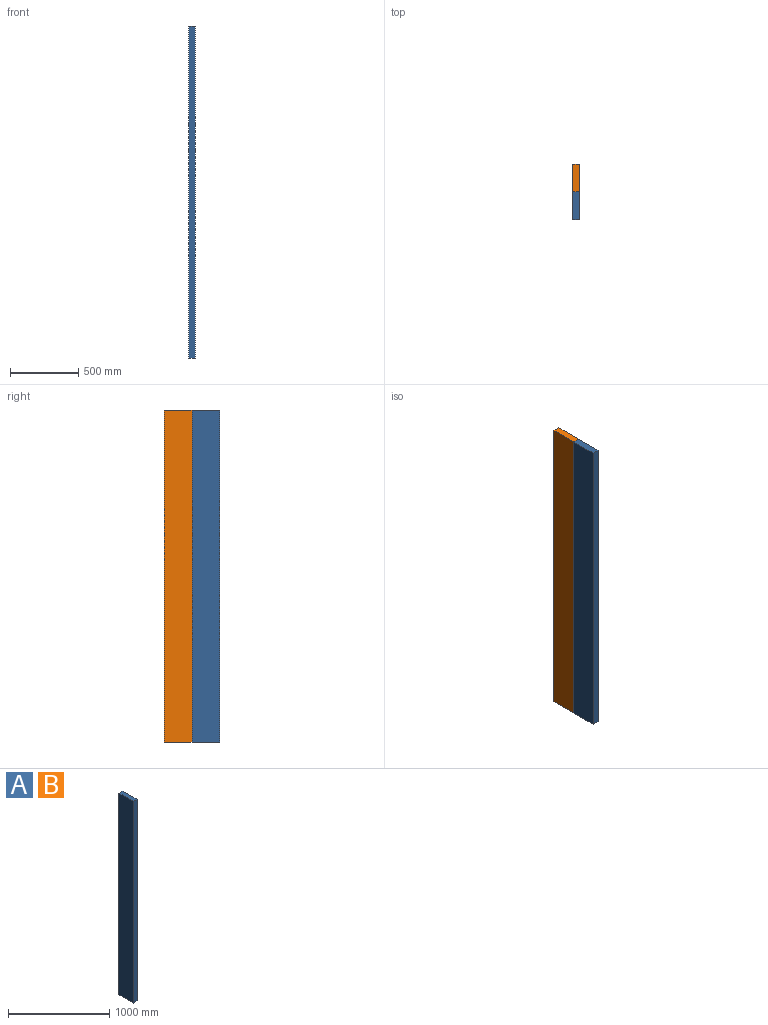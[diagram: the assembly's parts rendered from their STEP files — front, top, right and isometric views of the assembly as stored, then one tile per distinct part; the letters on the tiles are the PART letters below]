
ASSEMBLY  parts=2 mates=1
PART A: 6 faces, bbox 50.8x203.2x2438.4 mm
  f0: plane 203.2x50.8mm, normal (0,0,1), area 10322.6mm2, adj f1,f3,f4,f5
  f1: plane 2438.4x50.8mm, normal (0,-1,0), area 123870.7mm2, adj f0,f2,f4,f5
  f2: plane 203.2x50.8mm, normal (0,0,-1), area 10322.6mm2, adj f1,f3,f4,f5
  f3: plane 2438.4x50.8mm, normal (0,1,0), area 123870.7mm2, adj f0,f2,f4,f5
  f4: plane 2438.4x203.2mm, normal (1,0,0), area 495482.9mm2, adj f0,f1,f2,f3
  f5: plane 2438.4x203.2mm, normal (-1,0,0), area 495482.9mm2, adj f0,f1,f2,f3
PART B: same geometry as A
PLACE A t=(-398.45,-889.51,-1540.02)mm
PLACE B t=(-398.45,-686.31,-1540.02)mm
MATE fastened B.f1 <-> A.f3  axis (0,-1,0) through (-347.65,-991.72,-319.95)mm
